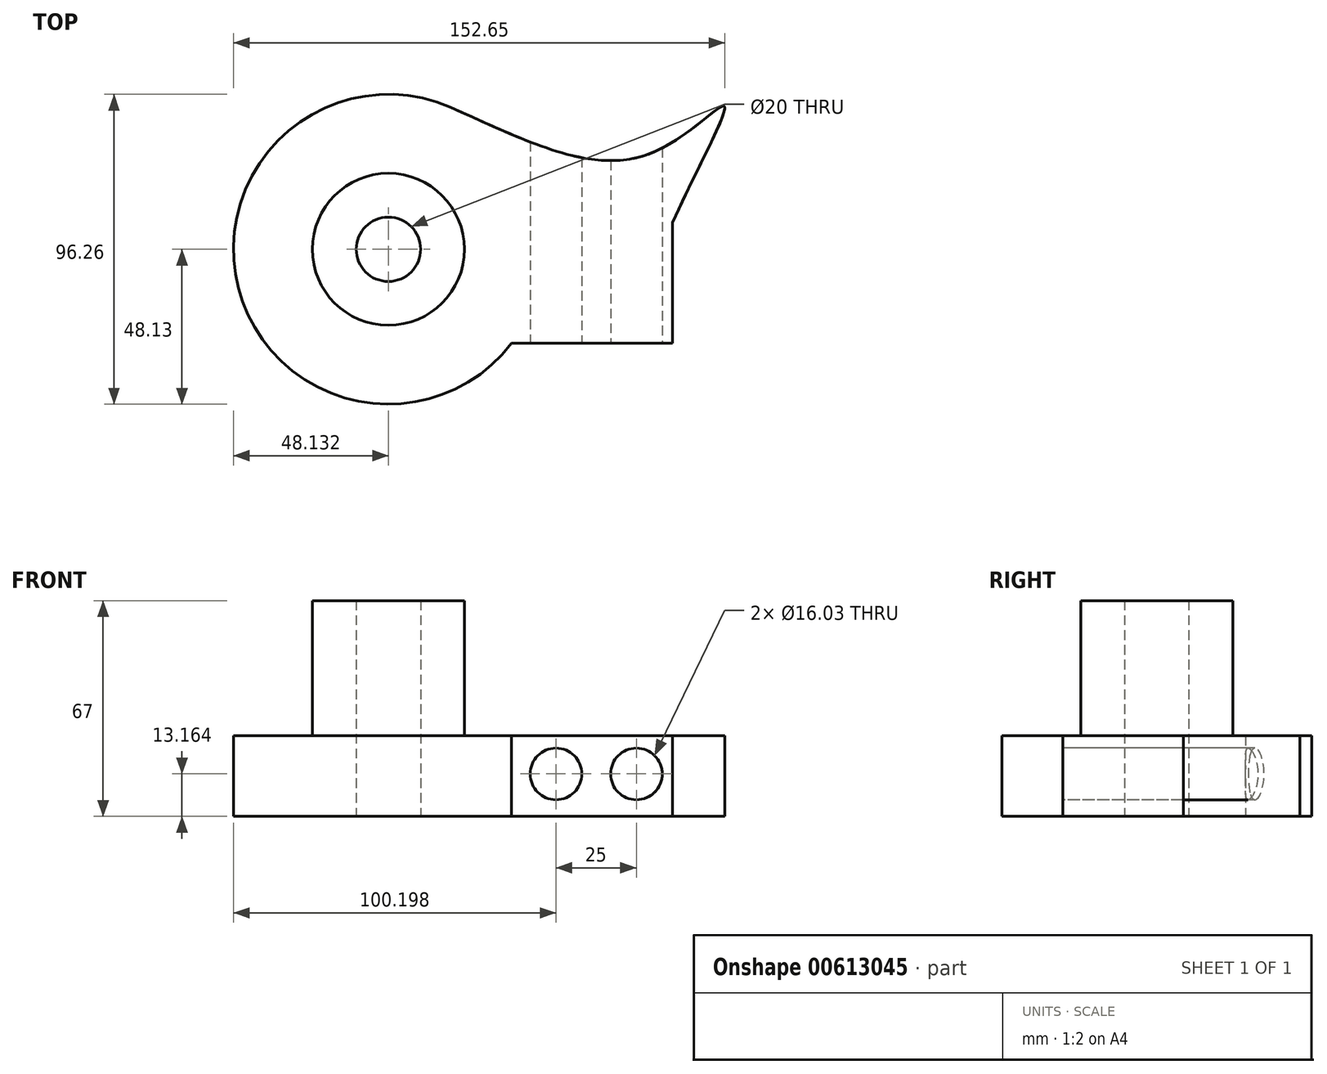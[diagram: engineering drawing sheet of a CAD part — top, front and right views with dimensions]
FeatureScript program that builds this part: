
annotation { "Feature Type Name" : "Feature", "Feature Type Description" : "" }
export const myFeature = defineFeature(function(context is Context, id is Id, definition is map)
    precondition{}
    {
        {
            var Q0;
            Q0=qCreatedBy(makeId("Top.planeOp"),FACE);
            var sketch = newSketch(context, id + "F0", { "sketchPlane" : qUnion([Q0])});
            skLineSegment(sketch, "E0.bottom", {"start": v(-44.14, 29.15) * mm, "end": v(44.14, 29.15) * mm});
            skLineSegment(sketch, "E0.top", {"start": v(-44.14, -29.15) * mm, "end": v(44.14, -29.15) * mm});
            skLineSegment(sketch, "E0.left", {"start": v(-44.14, 29.15) * mm, "end": v(-44.14, -29.15) * mm});
            skLineSegment(sketch, "E0.right", {"start": v(44.14, 29.15) * mm, "end": v(44.14, -29.15) * mm});
            skPoint(sketch, "E0.middle", {"position": v(0, 0) * mm});
            skCircle(sketch, "E1", {"center": v(-44.14, 0) * mm, "radius": 48.13 * mm});
            skCircle(sketch, "E2", {"center": v(-44.14, 0) * mm, "radius": 10 * mm});
            skFitSpline(sketch, "E3", {"points": [v(-24.82, 44.08) * mm, v(35.54, 29.15) * mm, v(60.1, 44.48) * mm, v(44.14, 8.34) * mm], "startDerivative": vector(162.62, -71.26) * mm, "endDerivative": vector(-75.65, -166.29) * mm});
            skCircle(sketch, "E4", {"center": v(-44.14, 0) * mm, "radius": 23.61 * mm});
            skSolve(sketch);
        }
        {
            var Q0;
            {var subQ0=sQuery(id+"F0.wireOp",EDGE,"E0.left");var subQ5=sQuery(id+"F0.wireOp",EDGE,"E0.bottom");var subQ6=makeQuery(id+"F0.imprint","INTERSECT",VERTEX,{"derivedFrom":[subQ5,subQ0]});Q0=makeQuery(id+"F0.imprint","IMPRINT",FACE,{"disambiguationData":[TD([[makeQuery(id+"F0.imprint","IMPRINT",EDGE,{"disambiguationData":[TD([[subQ6,-1.0]])],"derivedFrom":subQ5}),1.0]])]});}
            var Q1;
            {var subQ1=sQuery(id+"F0.wireOp",EDGE,"E0.bottom");var subQ3=sQuery(id+"F0.wireOp",EDGE,"E3");var subQ10=makeQuery(id+"F0.imprint","INTERSECT",VERTEX,{"disambiguationData":[OD(0.0)],"derivedFrom":[subQ1,subQ3]});Q1=makeQuery(id+"F0.imprint","IMPRINT",FACE,{"disambiguationData":[TD([[makeQuery(id+"F0.imprint","IMPRINT",EDGE,{"disambiguationData":[TD([[subQ10,1.0]])],"derivedFrom":subQ1}),-1.0]])]});}
            var Q2;
            {var subQ0=sQuery(id+"F0.wireOp",EDGE,"E0.right");var subQ1=sQuery(id+"F0.wireOp",EDGE,"E0.bottom");var subQ2=makeQuery(id+"F0.imprint","INTERSECT",VERTEX,{"derivedFrom":[subQ1,subQ0]});Q2=makeQuery(id+"F0.imprint","IMPRINT",FACE,{"disambiguationData":[TD([[makeQuery(id+"F0.imprint","IMPRINT",EDGE,{"disambiguationData":[TD([[subQ2,1.0]])],"derivedFrom":subQ1}),1.0]])]});}
            var Q3;
            {var subQ0=sQuery(id+"F0.wireOp",EDGE,"E3");var subQ1=sQuery(id+"F0.wireOp",EDGE,"E0.bottom");var subQ2=makeQuery(id+"F0.imprint","INTERSECT",VERTEX,{"disambiguationData":[OD(0.0)],"derivedFrom":[subQ1,subQ0]});Q3=makeQuery(id+"F0.imprint","IMPRINT",FACE,{"disambiguationData":[TD([[makeQuery(id+"F0.imprint","IMPRINT",EDGE,{"disambiguationData":[TD([[subQ2,1.0]])],"derivedFrom":subQ1}),1.0]])]});}
            var Q4;
            {var subQ0=sQuery(id+"F0.wireOp",EDGE,"E0.left");var subQ5=sQuery(id+"F0.wireOp",EDGE,"E0.bottom");var subQ6=makeQuery(id+"F0.imprint","INTERSECT",VERTEX,{"derivedFrom":[subQ5,subQ0]});Q4=makeQuery(id+"F0.imprint","IMPRINT",FACE,{"disambiguationData":[TD([[makeQuery(id+"F0.imprint","IMPRINT",EDGE,{"disambiguationData":[TD([[subQ6,-1.0]])],"derivedFrom":subQ5}),-1.0]])]});}
            extrude(context, id + "F1", {"entities" : qUnion([Q0, Q1, Q2, Q3, Q4]), "depth" : 25 * mm, "offsetDistance" : 25 * mm});
        }
        {
            var Q0;
            {var subQ0=sQuery(id+"F0.wireOp",EDGE,"E4");var subQ1=sQuery(id+"F0.wireOp",EDGE,"E0.left");var subQ2=makeQuery(id+"F0.imprint","INTERSECT",VERTEX,{"disambiguationData":[OD(0.0)],"derivedFrom":[subQ1,subQ0]});Q0=makeQuery(id+"F0.imprint","IMPRINT",FACE,{"disambiguationData":[TD([[makeQuery(id+"F0.imprint","IMPRINT",EDGE,{"disambiguationData":[TD([[subQ2,-1.0]])],"derivedFrom":subQ1}),-1.0]])]});}
            var Q1;
            {var subQ0=sQuery(id+"F0.wireOp",EDGE,"E4");var subQ1=sQuery(id+"F0.wireOp",EDGE,"E0.left");var subQ2=makeQuery(id+"F0.imprint","INTERSECT",VERTEX,{"disambiguationData":[OD(0.0)],"derivedFrom":[subQ1,subQ0]});Q1=makeQuery(id+"F0.imprint","IMPRINT",FACE,{"disambiguationData":[TD([[makeQuery(id+"F0.imprint","IMPRINT",EDGE,{"disambiguationData":[TD([[subQ2,-1.0]])],"derivedFrom":subQ1}),1.0]])]});}
            extrude(context, id + "F2", {"entities" : qUnion([Q0, Q1]), "operationType" : NewBodyOperationType.ADD, "depth" : 67 * mm, "offsetDistance" : 25 * mm});
        }
        {
            var Q0;
            Q0=makeQuery(id+"F1.opExtrude","SWEPT_FACE",FACE,{"disambiguationData":[OSD([sQuery(id+"F0.wireOp",EDGE,"E0.top")])]});
            var sketch = newSketch(context, id + "F3", { "sketchPlane" : qUnion([Q0])});
            skCircle(sketch, "E5", {"center": v(7.93, 13.16) * mm, "radius": 8.02 * mm});
            skCircle(sketch, "E6.1.0.0", {"center": v(32.93, 13.16) * mm, "radius": 8.02 * mm});
            skLineSegment(sketch, "E6.direction1", {"start": v(7.93, 13.16) * mm, "end": v(32.93, 13.16) * mm, "construction": true});
            skSolve(sketch);
        }
        {
            var Q0;
            Q0 = qSketchRegion(id + "F3", true);
            extrude(context, id + "F4", {"entities" : qUnion([Q0]), "operationType" : NewBodyOperationType.REMOVE, "endBound" : BoundingType.THROUGH_ALL, "oppositeDirection" : true, "depth" : 25 * mm, "offsetDistance" : 25 * mm});
        }
    });
